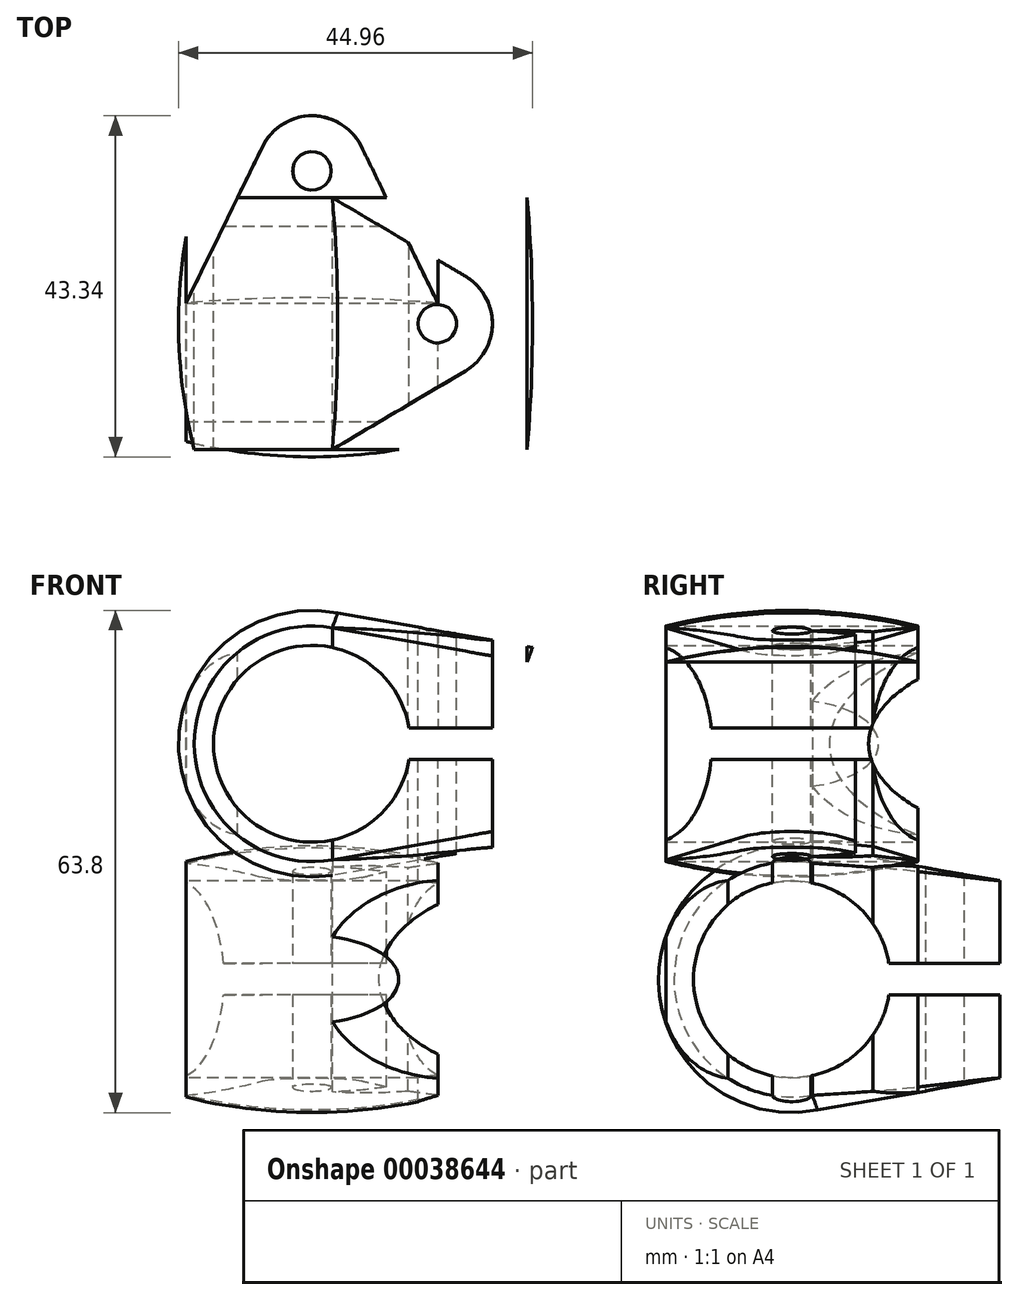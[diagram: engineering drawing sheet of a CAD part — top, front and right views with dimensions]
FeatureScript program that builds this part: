
annotation { "Feature Type Name" : "Feature", "Feature Type Description" : "" }
export const myFeature = defineFeature(function(context is Context, id is Id, definition is map)
    precondition{}
    {
        {
            var Q0;
            Q0=qCreatedBy(makeId("Right.planeOp"),FACE);
            var sketch = newSketch(context, id + "F0", { "sketchPlane" : qUnion([Q0])});
            skArc(sketch, "E0", {"start": v(2.6, 14.73) * mm, "mid": v(-14.96, 0) * mm, "end": v(2.6, -14.73) * mm});
            skArc(sketch, "E1", {"start": v(12.34, 2) * mm, "mid": v(-12.5, 0) * mm, "end": v(12.34, -2) * mm});
            skLineSegment(sketch, "E2", {"start": v(0, 0) * mm, "end": v(62.19, 0) * mm, "construction": true});
            skLineSegment(sketch, "E3", {"start": v(0, 0) * mm, "end": v(0, -5.05) * mm, "construction": true});
            skLineSegment(sketch, "E4", {"start": v(12.34, 2) * mm, "end": v(27.34, 2) * mm});
            skLineSegment(sketch, "E5", {"start": v(12.34, -2) * mm, "end": v(27.34, -2) * mm});
            skLineSegment(sketch, "E6", {"start": v(27.34, -10.37) * mm, "end": v(2.6, -14.73) * mm});
            skLineSegment(sketch, "E7", {"start": v(2.6, 14.73) * mm, "end": v(27.34, 10.37) * mm});
            skLineSegment(sketch, "E8", {"start": v(27.34, 10.37) * mm, "end": v(27.34, 2) * mm});
            skLineSegment(sketch, "E9.trimOffspring", {"start": v(27.34, -2) * mm, "end": v(27.34, -10.37) * mm});
            skLineSegment(sketch, "E10", {"start": v(0, 0) * mm, "end": v(0, 11.68) * mm, "construction": true});
            skLineSegment(sketch, "E11", {"start": v(27.34, -10.37) * mm, "end": v(27.34, 40.43) * mm, "construction": true});
            skLineSegment(sketch, "E12", {"start": v(2.17, 12.31) * mm, "end": v(27.34, 7.87) * mm});
            skLineSegment(sketch, "E13", {"start": v(27.34, -7.87) * mm, "end": v(2.17, -12.31) * mm});
            skLineSegment(sketch, "E14", {"start": v(-34.62, 14.96) * mm, "end": v(41.46, 14.96) * mm, "construction": true});
            skPoint(sketch, "E15.orphan", {"position": v(0, 14.96) * mm});
            skSolve(sketch);
        }
        {
            var Q0;
            {var subQ2=sQuery(id+"F0.wireOp",EDGE,"E4");Q0=makeQuery(id+"F0.imprint","IMPRINT",FACE,{"disambiguationData":[TD([[makeQuery(id+"F0.imprint","IMPRINT",EDGE,{"derivedFrom":subQ2}),1.0]])]});}
            var Q1;
            Q1=makeQuery(id+"F0.imprint","IMPRINT",FACE,{"disambiguationData":[TD([[makeQuery(id+"F0.imprint","IMPRINT",EDGE,{"derivedFrom":sQuery(id+"F0.wireOp",EDGE,"E0")}),1.0]])]});
            var Q2;
            {var subQ2=sQuery(id+"F0.wireOp",EDGE,"E5");Q2=makeQuery(id+"F0.imprint","IMPRINT",FACE,{"disambiguationData":[TD([[makeQuery(id+"F0.imprint","IMPRINT",EDGE,{"derivedFrom":subQ2}),-1.0]])]});}
            extrude(context, id + "F1", {"entities" : qUnion([Q0, Q1, Q2]), "endBound" : BoundingType.SYMMETRIC, "depth" : 32 * mm});
        }
        {
            var Q0;
            Q0=makeQuery(id+"F1.opExtrude","SWEPT_FACE",FACE,{"disambiguationData":[OSD([sQuery(id+"F0.wireOp",EDGE,"E8")])]});
            var sketch = newSketch(context, id + "F2", { "sketchPlane" : qUnion([Q0])});
            skArc(sketch, "E16", {"start": v(16, 10.37) * mm, "mid": v(0, 12.37) * mm, "end": v(-16, 10.37) * mm});
            skSolve(sketch);
        }
        {
            var Q0;
            Q0=makeQuery(id+"F2.imprint","IMPRINT",FACE,{"disambiguationData":[TD([[makeQuery(id+"F2.imprint","IMPRINT",EDGE,{"derivedFrom":sQuery(id+"F2.wireOp",EDGE,"E16")}),1.0]])]});
            var Q1;
            Q1=makeQuery(id+"F1.opExtrude","CAP_EDGE",EDGE,{"disambiguationData":[OSD([sQuery(id+"F0.wireOp",EDGE,"E7")])],"isStart":false});
            var Q2;
            Q2=makeQuery(id+"F1.opExtrude","CAP_EDGE",EDGE,{"disambiguationData":[OSD([sQuery(id+"F0.wireOp",EDGE,"E0")])],"isStart":false});
            var Q3;
            Q3=makeQuery(id+"F1.opExtrude","CAP_EDGE",EDGE,{"disambiguationData":[OSD([sQuery(id+"F0.wireOp",EDGE,"E6")])],"isStart":false});
            sweep(context, id + "F3", {"operationType" : NewBodyOperationType.ADD, "profiles" : qUnion([Q0]), "path" : qUnion([Q1, Q2, Q3])});
        }
        {
            var Q0;
            Q0=qCreatedBy(makeId("Front.planeOp"),FACE);
            var sketch = newSketch(context, id + "F4", { "sketchPlane" : qUnion([Q0])});
            skArc(sketch, "E17", {"start": v(2.6, 44.66) * mm, "mid": v(-14.96, 29.92) * mm, "end": v(2.6, 15.19) * mm});
            skArc(sketch, "E18", {"start": v(12.34, 31.92) * mm, "mid": v(-12.5, 29.92) * mm, "end": v(12.34, 27.92) * mm});
            skLineSegment(sketch, "E19", {"start": v(0, 29.92) * mm, "end": v(50.91, 29.92) * mm, "construction": true});
            skLineSegment(sketch, "E20", {"start": v(0, 53.44) * mm, "end": v(0, 29.92) * mm, "construction": true});
            skLineSegment(sketch, "E21", {"start": v(12.34, 31.92) * mm, "end": v(27.34, 31.92) * mm});
            skLineSegment(sketch, "E22", {"start": v(12.34, 27.92) * mm, "end": v(27.34, 27.92) * mm});
            skLineSegment(sketch, "E23", {"start": v(27.34, 19.55) * mm, "end": v(2.6, 15.19) * mm});
            skLineSegment(sketch, "E24", {"start": v(2.6, 44.66) * mm, "end": v(27.34, 40.3) * mm});
            skLineSegment(sketch, "E25", {"start": v(27.34, 40.3) * mm, "end": v(27.34, 31.92) * mm});
            skLineSegment(sketch, "E26.trimOffspring", {"start": v(27.34, 27.92) * mm, "end": v(27.34, 19.55) * mm});
            skLineSegment(sketch, "E27", {"start": v(0, 29.92) * mm, "end": v(0, 41.6) * mm, "construction": true});
            skLineSegment(sketch, "E28", {"start": v(27.34, 19.55) * mm, "end": v(27.34, 70.35) * mm, "construction": true});
            skLineSegment(sketch, "E29", {"start": v(2.17, 42.23) * mm, "end": v(27.34, 37.8) * mm});
            skLineSegment(sketch, "E30", {"start": v(27.34, 22.05) * mm, "end": v(2.17, 17.61) * mm});
            skLineSegment(sketch, "E31", {"start": v(0, 0) * mm, "end": v(0, 59.85) * mm, "construction": true});
            skLineSegment(sketch, "E32", {"start": v(-29.29, 14.96) * mm, "end": v(50.58, 14.96) * mm, "construction": true});
            skPoint(sketch, "E33.orphan", {"position": v(0, 14.96) * mm});
            skSolve(sketch);
        }
        {
            var Q0;
            {var subQ1=sQuery(id+"F4.wireOp",EDGE,"E21");Q0=makeQuery(id+"F4.imprint","IMPRINT",FACE,{"disambiguationData":[TD([[makeQuery(id+"F4.imprint","IMPRINT",EDGE,{"derivedFrom":subQ1}),1.0]])]});}
            var Q1;
            Q1=makeQuery(id+"F4.imprint","IMPRINT",FACE,{"disambiguationData":[TD([[makeQuery(id+"F4.imprint","IMPRINT",EDGE,{"derivedFrom":sQuery(id+"F4.wireOp",EDGE,"E17")}),1.0]])]});
            var Q2;
            {var subQ2=sQuery(id+"F4.wireOp",EDGE,"E22");Q2=makeQuery(id+"F4.imprint","IMPRINT",FACE,{"disambiguationData":[TD([[makeQuery(id+"F4.imprint","IMPRINT",EDGE,{"derivedFrom":subQ2}),-1.0]])]});}
            extrude(context, id + "F5", {"entities" : qUnion([Q0, Q1, Q2]), "endBound" : BoundingType.SYMMETRIC, "depth" : 32 * mm});
        }
        {
            var Q0;
            Q0=makeQuery(id+"F5.opExtrude","SWEPT_FACE",FACE,{"disambiguationData":[OSD([sQuery(id+"F4.wireOp",EDGE,"E26.trimOffspring")])]});
            var sketch = newSketch(context, id + "F6", { "sketchPlane" : qUnion([Q0])});
            skArc(sketch, "E34", {"start": v(-16, 19.55) * mm, "mid": v(0, 17.55) * mm, "end": v(16, 19.55) * mm});
            skLineSegment(sketch, "E35", {"start": v(-16, 19.55) * mm, "end": v(16, 19.55) * mm});
            skSolve(sketch);
        }
        {
            var Q0;
            Q0=makeQuery(id+"F6.imprint","IMPRINT",FACE,{"disambiguationData":[TD([[makeQuery(id+"F6.imprint","IMPRINT",EDGE,{"derivedFrom":sQuery(id+"F6.wireOp",EDGE,"E34")}),1.0]])]});
            var Q1;
            Q1=makeQuery(id+"F5.opExtrude","CAP_EDGE",EDGE,{"disambiguationData":[OSD([sQuery(id+"F4.wireOp",EDGE,"E24")])],"isStart":false});
            var Q2;
            Q2=makeQuery(id+"F5.opExtrude","CAP_EDGE",EDGE,{"disambiguationData":[OSD([sQuery(id+"F4.wireOp",EDGE,"E17")])],"isStart":false});
            var Q3;
            Q3=makeQuery(id+"F5.opExtrude","CAP_EDGE",EDGE,{"disambiguationData":[OSD([sQuery(id+"F4.wireOp",EDGE,"E23")])],"isStart":false});
            sweep(context, id + "F7", {"profiles" : qUnion([Q0]), "path" : qUnion([Q1, Q2, Q3])});
        }
        {
            var Q0;
            Q0=makeQuery(id+"F1.opExtrude","SWEPT_FACE",FACE,{"disambiguationData":[OSD([sQuery(id+"F0.wireOp",EDGE,"E4")])]});
            cPlane(context, id + "F8", {"entities" : qUnion([Q0]), "cplaneType" : CPlaneType.OFFSET, "offset" : 150 * mm, "width" : 150 * mm, "height" : 150 * mm});
        }
        {
            var Q0;
            Q0=qCreatedBy(id+"F8.planeOp",FACE);
            var sketch = newSketch(context, id + "F9", { "sketchPlane" : qUnion([Q0])});
            skCircle(sketch, "E36", {"center": v(0, -19.4) * mm, "radius": 5 * mm});
            skCircle(sketch, "E37", {"center": v(0, -19.4) * mm, "radius": 2.45 * mm});
            skLineSegment(sketch, "E38", {"start": v(-16, -31.17) * mm, "end": v(16, -31.17) * mm});
            skCircle(sketch, "E39", {"center": v(0, -19.4) * mm, "radius": 7 * mm});
            skLineSegment(sketch, "E40", {"start": v(6.29, -22.48) * mm, "end": v(16, -2.6) * mm});
            skLineSegment(sketch, "E41", {"start": v(-6.29, -22.48) * mm, "end": v(-16, -2.6) * mm});
            skLineSegment(sketch, "E42", {"start": v(-16, -2.6) * mm, "end": v(-16, -31.17) * mm});
            skLineSegment(sketch, "E43", {"start": v(16, -31.17) * mm, "end": v(16, -2.6) * mm});
            skSolve(sketch);
        }
        {
            var Q0;
            Q0=makeQuery(id+"F9.imprint","IMPRINT",FACE,{"disambiguationData":[TD([[makeQuery(id+"F9.imprint","IMPRINT",EDGE,{"derivedFrom":sQuery(id+"F9.wireOp",EDGE,"E38")}),1.0]])]});
            var Q1;
            Q1=makeQuery(id+"F9.imprint","IMPRINT",FACE,{"disambiguationData":[TD([[makeQuery(id+"F9.imprint","IMPRINT",EDGE,{"derivedFrom":sQuery(id+"F9.wireOp",EDGE,"E37")}),1.0]])]});
            extrude(context, id + "F10", {"entities" : qUnion([Q0, Q1]), "operationType" : NewBodyOperationType.REMOVE, "oppositeDirection" : true, "depth" : 192.56 * mm, "hasSecondDirection" : true, "secondDirectionOppositeDirection" : true, "secondDirectionDepth" : 25 * mm});
        }
        {
            var Q0;
            Q0=makeQuery(id+"F5.opExtrude","SWEPT_FACE",FACE,{"disambiguationData":[OSD([sQuery(id+"F4.wireOp",EDGE,"E22")])]});
            cPlane(context, id + "F11", {"entities" : qUnion([Q0]), "cplaneType" : CPlaneType.OFFSET, "offset" : 150 * mm, "width" : 150 * mm, "height" : 150 * mm});
        }
        {
            var Q0;
            Q0=qCreatedBy(id+"F11.planeOp",FACE);
            var sketch = newSketch(context, id + "F12", { "sketchPlane" : qUnion([Q0])});
            skCircle(sketch, "E44", {"center": v(15.92, 0) * mm, "radius": 5 * mm});
            skCircle(sketch, "E45", {"center": v(15.92, 0) * mm, "radius": 2.45 * mm});
            skLineSegment(sketch, "E46", {"start": v(27.34, -16) * mm, "end": v(27.34, 16) * mm});
            skCircle(sketch, "E47", {"center": v(15.92, 0) * mm, "radius": 7 * mm});
            skLineSegment(sketch, "E48", {"start": v(19.48, 6.03) * mm, "end": v(2.6, 16) * mm});
            skLineSegment(sketch, "E49", {"start": v(19.48, -6.03) * mm, "end": v(2.6, -16) * mm});
            skLineSegment(sketch, "E50", {"start": v(2.6, -16) * mm, "end": v(27.34, -16) * mm});
            skLineSegment(sketch, "E51", {"start": v(27.34, 16) * mm, "end": v(2.6, 16) * mm});
            skSolve(sketch);
        }
        {
            var Q0;
            Q0=makeQuery(id+"F12.imprint","IMPRINT",FACE,{"disambiguationData":[TD([[makeQuery(id+"F12.imprint","IMPRINT",EDGE,{"derivedFrom":sQuery(id+"F12.wireOp",EDGE,"E46")}),1.0]])]});
            var Q1;
            Q1=makeQuery(id+"F12.imprint","IMPRINT",FACE,{"disambiguationData":[TD([[makeQuery(id+"F12.imprint","IMPRINT",EDGE,{"derivedFrom":sQuery(id+"F12.wireOp",EDGE,"E45")}),1.0]])]});
            var Q2;
            Q2=makeQuery(id+"F5.opExtrude","SWEPT_BODY",BODY,{"disambiguationData":[OSD([sQuery(id+"F4.wireOp",EDGE,"E17"),sQuery(id+"F4.wireOp",EDGE,"E18"),sQuery(id+"F4.wireOp",EDGE,"E21"),sQuery(id+"F4.wireOp",EDGE,"E22"),sQuery(id+"F4.wireOp",EDGE,"E23"),sQuery(id+"F4.wireOp",EDGE,"E24"),sQuery(id+"F4.wireOp",EDGE,"E25"),sQuery(id+"F4.wireOp",EDGE,"E26.trimOffspring")])]});
            extrude(context, id + "F13", {"entities" : qUnion([Q0, Q1]), "operationType" : NewBodyOperationType.REMOVE, "oppositeDirection" : true, "endBoundEntityBody" : qUnion([Q2]), "depth" : 195.48 * mm});
        }
    });
